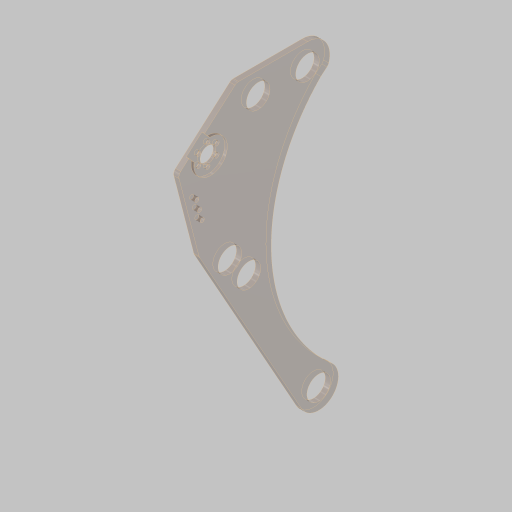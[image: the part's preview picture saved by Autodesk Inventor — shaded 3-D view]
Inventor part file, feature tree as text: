
AUTODESK INVENTOR PART (.ipt)
format: ipt  version: 2023.5 (Build 275446000, 446)  size: 258,048 bytes
history: native  units: in
note: dims shown in document units (in); Inventor stores cm internally (conversion verified against a paired STEP export)
features: sketch x7, extrude x4, projected_geometry x4, hole x2, fillet x1
ambient origin geometry x8: Origin, YZ Plane, XZ Plane, XY Plane, X Axis, Y Axis, Z Axis, Center Point
bodies: Body1 (feature_tree)
feature tree (18):
  sketch  "Sketch1"  dims[d0=16.0in d1=3.0in]
  extrude  "Extrusion2"  Depth=3.0in
  hole  "Hole2"  [1 undecoded]
  extrude  "Extrusion3"  Depth=7.0in
  fillet  "Fillet1"  Radius=1.125in
  extrude  "Extrusion4"  Depth=0.375in
  extrude  "Extrusion5"  Depth=3.75in
  hole  "Hole4"  [1 undecoded]
  sketch  "Sketch4"  dims[d2=0.25in d4=4.5in]
  sketch  "Sketch5"  dims[d5=11.875in d6=7.0in d27=1.125in]
  sketch  "Sketch6"  dims[d29=0.375in d31=4.0in]
  projected_geometry  "Projected Loop1"
  sketch  "Sketch8"  dims[d33=4.0in d35=3.75in]
  sketch  "Sketch9"  dims[d36=0.25in d37=0.0in d39=0.5in]
  sketch  "Sketch10"  dims[d41=0.201in d42=0.75in d43=0.385in d44=0.25in d45=0.5635in d46=1.0in d47=0.8108in d51=6.5in d52=11.0in d53=1.2075in d57=1.0in d58=11.75in d59=12.75in d60=1.25in d63=1.0in d64=0.0in d65=0.5in d66=0.26in d76=0.602in d77=1.5in d78=2.256in d79=2.6463in d80=1.5in d81=1.0in d82=2.3514in d83=0.75in d84=1.125in d85=6.2598in d87=1.4in d88=7.1457in d90=1.0in d91=0.0in d92=1.125in d93=1.6in d94=0.125in d95=0.0in d96=1.0in d97=1.0in d98=2.3622in d100=360.0deg d102=0.201in d103=0.198in d104=0.385in d105=0.25in d106=0.5635in d107=1.0in d108=0.8108in]
  projected_geometry  "Project Cut Edges1"
  projected_geometry  "Project Cut Edges2"
  projected_geometry  "Project Cut Edges3"
note: 2 required parameter values undecoded (feature->parameter linkage not recoverable at this tier; creation-order binding heuristic only, values carry confidence <= 0.55)
